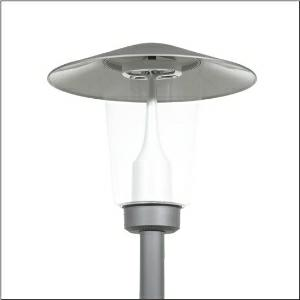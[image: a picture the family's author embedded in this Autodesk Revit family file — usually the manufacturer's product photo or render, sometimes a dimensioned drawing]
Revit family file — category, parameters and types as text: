
# Revit family: pilzleuchte_iq___st1_2a_5xa5235af14hp_844e
name_source: partatom
category: Lighting Fixtures
units: mm (PartAtom-declared; Revit-internal decimal feet)

## family parameters
Cut with Voids When Loaded = No
Host = Face
Light Source = No
Part Type = Normal
Room Calculation Point = No
Round Connector Dimension = Use Diameter
Shared = No

## types (1)
- --- (1 x LED, 3950 lm, 33.6 W, 2200K)
    Apparent Load = 34 VA
    CIE Flux Codes = 23 60 92 98 100
    Color Rendering = 70
    Color Temperature = 2200K
    Default Elevation = 1800 mm
    Description = Mushroom Luminaire iQ, mast luminaire, Module 540 iQ-SR, primary light control with 3 zone facetted reflector, of plastic, silver coated, highly specular, structured, primary optical cover: cover, of PMMA, transparent, light distribution: ST1.2a, light emission: direct distribution, primary light characteristic: asymmetric, installation type: post-top, LED, High Power LED, rated luminous flux: 3.950lm, luminous efficacy: 117lm/W, light colour: 722, colour temperature: 2200K, control gear: iQ Street-Remote, control: pre-setting: logarithmic dimming characteristic, Street-Remote, Auto-Match, Temp-Guard, Lumen-Switch, Night-Set, Smart-Wire, Light-Fading, Desk-Remote (wireless, voltage-free reading and setting of iQ features in the workshop via application-optimized NFC function/RFID function), optimised constant luminous flux control (CLO 2.0), with terminal, 6-pole, max. 2.5mm², mains connection: 230..240V, AC, 50/60Hz, start of lifetime: 34W, end of service life: 36W, reduction: 15W, luminaire housing, upper part, of glass-fibre reinforced polyester, coated, Siteco® metallic grey (DB 702S), diameter: 650mm, height: 586mm, spigot size: d x l = 76 x 70mm (post-top) | with reducer (optional accessory) 60 x 70mm, mounting height: 3..5m, post-top mast mounting element, of diecast aluminium, coated, Siteco® metallic grey (DB 702S), Module 540 iQ-SR, traffic white (RAL 9016), equipment: Power, protection rating (complete): IP65, insulation class (complete): insulation class II (safety insulation), certification: CE, ENEC, VDE, packaging unit: 1 piece

Light Distribution: ST1.2a
    Height = 586 mm
    Lamp = 1 x LED
    Lamp Light Flux = 3950 lm
    Lamp Power = 33.6 W
    Lamp count = 1
    Length = 650 mm
    Luminous efficacy = 118 lm/W
    Manufacturer = Siteco
    ModVariant = No
    Model = 5XA5235AF14HP
    Number of Poles = 1
    OnlyDefault = Yes
    Power Factor = 1
    Product Name = Pilzleuchte iQ | ST1.2a
    Product group = mast luminaire | pylon top
    ProductGroupID = 6100
    Protection Class = Protection class II
    Protection Degree = IP 65
    RLX_Detail_Level = 1
    RLX_Emergency_Light_Flux = 0 lm
    RLX_Emergency_Type = 0
    RLX_Emergency_Type_DB = No
    RlxData = <blob elided: 51585 chars, md5=3ba6df04>
    Socket = socket
    Standby Power = 0 W
    System Light Flux = 3950 lm
    System Power = 34 W
    Type Comments = factory setting: luminous flux: 100 % | dim-lin: 254 | 695 mA
    Type Image = l_1006077.jpg
    URL = http://relux.com
    VarID = @adj_193658
    Voltage = 0 V
    Weight = 0.00 kg
    Width = 0 mm  [stored 0 ft]

note: [stored X ft] marks values corroborated as IEEE doubles in the binary element streams (Revit-internal decimal feet)

## geometry (parser evidence)
native form markers: Blend x4, Sweep x8
no freeform markers — native parametric forms only
